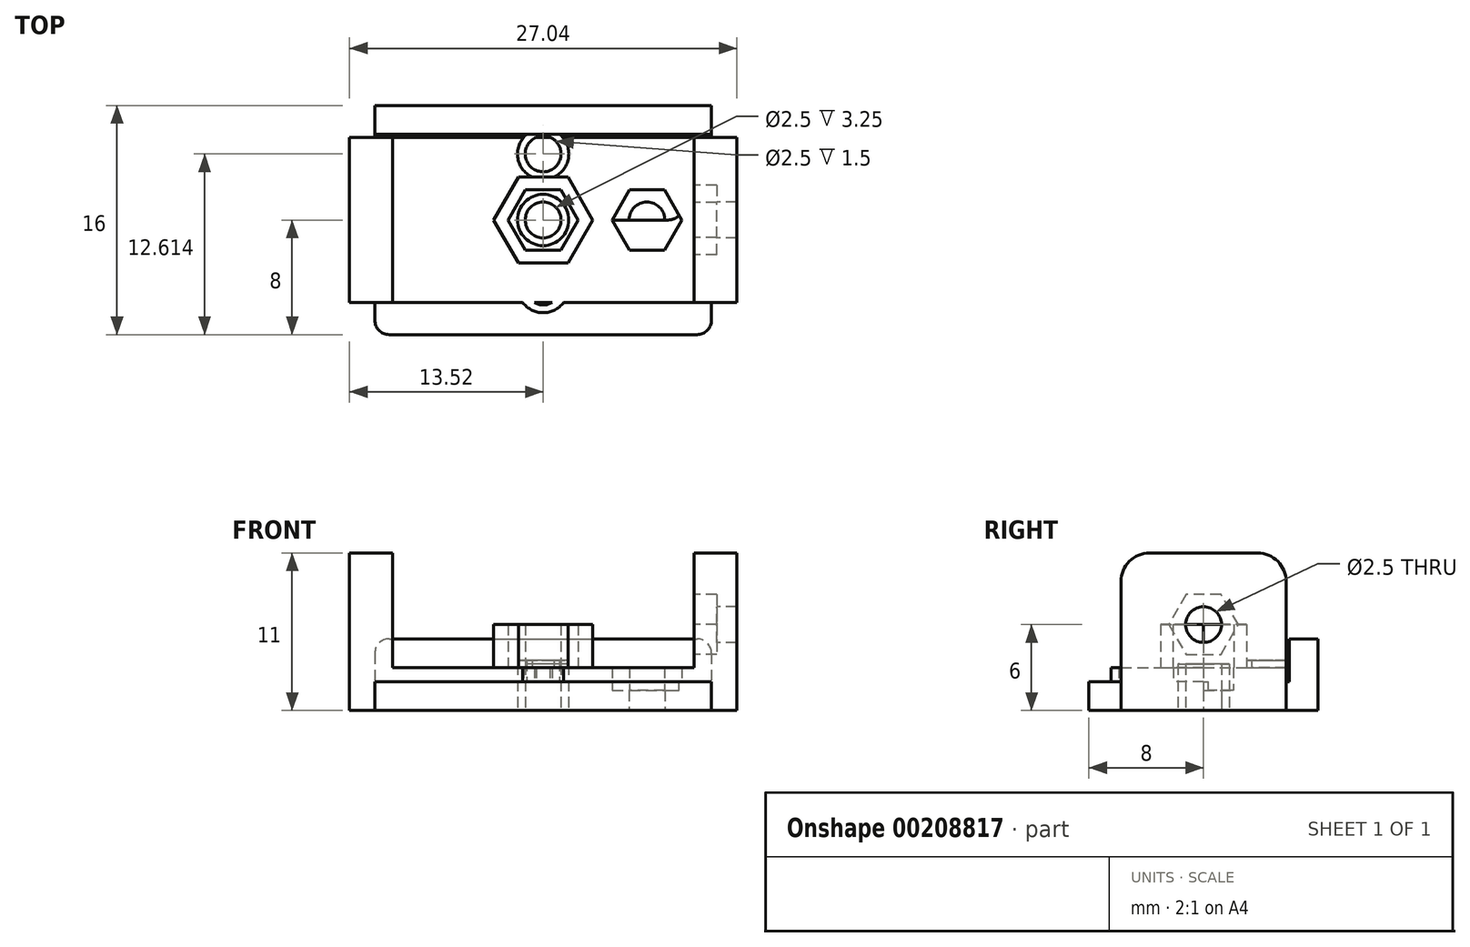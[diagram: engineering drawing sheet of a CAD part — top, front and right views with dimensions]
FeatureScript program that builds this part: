
annotation { "Feature Type Name" : "Feature", "Feature Type Description" : "" }
export const myFeature = defineFeature(function(context is Context, id is Id, definition is map)
    precondition{}
    {
        {
            var Q0;
            Q0=qCreatedBy(makeId("Top.planeOp"),FACE);
            var sketch = newSketch(context, id + "F0", { "sketchPlane" : qUnion([Q0])});
            skLineSegment(sketch, "E0.bottom", {"start": v(-11.75, 8) * mm, "end": v(11.75, 8) * mm});
            skLineSegment(sketch, "E0.top", {"start": v(-11.75, -8) * mm, "end": v(11.75, -8) * mm});
            skLineSegment(sketch, "E0.left", {"start": v(-11.75, 8) * mm, "end": v(-11.75, -8) * mm});
            skLineSegment(sketch, "E0.right", {"start": v(11.75, 8) * mm, "end": v(11.75, -8) * mm});
            skPoint(sketch, "E0.middle", {"position": v(0, 0) * mm});
            skLineSegment(sketch, "E1", {"start": v(-11.75, 6) * mm, "end": v(11.75, 6) * mm});
            skLineSegment(sketch, "E2.bottom", {"start": v(-9.75, 0) * mm, "end": v(9.75, 0) * mm});
            skLineSegment(sketch, "E2.top", {"start": v(-9.75, 2.5) * mm, "end": v(9.75, 2.5) * mm});
            skLineSegment(sketch, "E2.left", {"start": v(-9.75, 0) * mm, "end": v(-9.75, 2.5) * mm});
            skLineSegment(sketch, "E2.right", {"start": v(9.75, 0) * mm, "end": v(9.75, 2.5) * mm});
            skPoint(sketch, "E2.middle", {"position": v(0, 1.25) * mm});
            skCircle(sketch, "E3", {"center": v(0, 1.25) * mm, "radius": 1.1 * mm, "construction": true});
            skCircle(sketch, "E4", {"center": v(0, 1.25) * mm, "radius": 2.4 * mm, "construction": true});
            skCircle(sketch, "E5", {"center": v(0, 1.25) * mm, "radius": 1 * mm, "construction": true});
            skSolve(sketch);
        }
        {
            var Q0;
            {var subQ1=sQuery(id+"F0.wireOp",EDGE,"E0.top");Q0=makeQuery(id+"F0.imprint","IMPRINT",FACE,{"disambiguationData":[TD([[makeQuery(id+"F0.imprint","IMPRINT",EDGE,{"derivedFrom":subQ1}),1.0]])]});}
            extrude(context, id + "F1", {"entities" : qUnion([Q0]), "depth" : 2 * mm, "offsetDistance" : 25 * mm});
        }
        {
            var Q0;
            {var subQ0=sQuery(id+"F0.wireOp",EDGE,"E0.bottom");Q0=makeQuery(id+"F0.imprint","IMPRINT",FACE,{"disambiguationData":[TD([[makeQuery(id+"F0.imprint","IMPRINT",EDGE,{"derivedFrom":subQ0}),-1.0]])]});}
            extrude(context, id + "F2", {"entities" : qUnion([Q0]), "operationType" : NewBodyOperationType.ADD, "depth" : 5 * mm, "offsetDistance" : 25 * mm});
        }
        {
            var Q0;
            Q0=makeQuery(id+"F1.opExtrude","SWEPT_EDGE",EDGE,{"disambiguationData":[OSD([sQuery(id+"F0.wireOp",EDGE,"E2.top"),sQuery(id+"F0.wireOp",EDGE,"E2.left")])]});
            var Q1;
            Q1=makeQuery(id+"F1.opExtrude","SWEPT_EDGE",EDGE,{"disambiguationData":[OSD([sQuery(id+"F0.wireOp",EDGE,"E2.bottom"),sQuery(id+"F0.wireOp",EDGE,"E2.left")])]});
            var Q2;
            Q2=makeQuery(id+"F1.opExtrude","SWEPT_EDGE",EDGE,{"disambiguationData":[OSD([sQuery(id+"F0.wireOp",EDGE,"E2.top"),sQuery(id+"F0.wireOp",EDGE,"E2.right")])]});
            var Q3;
            Q3=makeQuery(id+"F1.opExtrude","SWEPT_EDGE",EDGE,{"disambiguationData":[OSD([sQuery(id+"F0.wireOp",EDGE,"E2.bottom"),sQuery(id+"F0.wireOp",EDGE,"E2.right")])]});
            var Q4;
            Q4=makeQuery(id+"F2.opExtrude","CAP_EDGE",EDGE,{"disambiguationData":[OSD([sQuery(id+"F0.wireOp",EDGE,"E0.right")])],"isStart":false});
            var Q5;
            Q5=makeQuery(id+"F2.opExtrude","CAP_EDGE",EDGE,{"disambiguationData":[OSD([sQuery(id+"F0.wireOp",EDGE,"E0.left")])],"isStart":false});
            var Q6;
            Q6=makeQuery(id+"F1.opExtrude","SWEPT_EDGE",EDGE,{"disambiguationData":[OSD([sQuery(id+"F0.wireOp",EDGE,"E0.top"),sQuery(id+"F0.wireOp",EDGE,"E0.left")])]});
            var Q7;
            Q7=makeQuery(id+"F1.opExtrude","SWEPT_EDGE",EDGE,{"disambiguationData":[OSD([sQuery(id+"F0.wireOp",EDGE,"E0.top"),sQuery(id+"F0.wireOp",EDGE,"E0.right")])]});
            fillet(context, id + "F3", {"entities" : qUnion([Q0, Q1, Q2, Q3, Q4, Q5, Q6, Q7]), "radius" : 1 * mm, "tangentPropagation" : true, "allowEdgeOverflow" : false});
        }
        {
            var Q0;
            Q0=qCreatedBy(makeId("Top.planeOp"),FACE);
            var sketch = newSketch(context, id + "F4", { "sketchPlane" : qUnion([Q0])});
            skLineSegment(sketch, "E6.bottom", {"start": v(-13.52, -5.77) * mm, "end": v(13.52, -5.77) * mm});
            skLineSegment(sketch, "E6.top", {"start": v(-13.52, 5.77) * mm, "end": v(13.52, 5.77) * mm});
            skLineSegment(sketch, "E6.left", {"start": v(-13.52, -5.77) * mm, "end": v(-13.52, 5.77) * mm});
            skLineSegment(sketch, "E6.right", {"start": v(13.52, -5.77) * mm, "end": v(13.52, 5.77) * mm});
            skPoint(sketch, "E6.middle", {"position": v(0, 0) * mm});
            skLineSegment(sketch, "E7", {"start": v(10.52, -5.77) * mm, "end": v(10.52, 5.77) * mm});
            skCircle(sketch, "E8", {"center": v(7.25, 0) * mm, "radius": 2.5 * mm, "construction": true});
            skCircle(sketch, "E9", {"center": v(7.25, 0) * mm, "radius": 1.25 * mm});
            skLineSegment(sketch, "E10.MirrorCS", {"start": v(-10.52, -5.77) * mm, "end": v(-10.52, 5.77) * mm});
            skCircle(sketch, "E11.cCircle", {"center": v(7.25, 0) * mm, "radius": 2.1 * mm, "construction": true});
            skLineSegment(sketch, "E11.0", {"start": v(8.46, -2.1) * mm, "end": v(6.03, -2.1) * mm});
            skLineSegment(sketch, "E11.1", {"start": v(6.03, -2.1) * mm, "end": v(4.82, 0) * mm});
            skLineSegment(sketch, "E11.2", {"start": v(4.82, 0) * mm, "end": v(6.03, 2.1) * mm});
            skLineSegment(sketch, "E11.3", {"start": v(6.03, 2.1) * mm, "end": v(8.46, 2.1) * mm});
            skLineSegment(sketch, "E11.4", {"start": v(8.46, 2.1) * mm, "end": v(9.67, 0) * mm});
            skLineSegment(sketch, "E11.5", {"start": v(9.67, 0) * mm, "end": v(8.46, -2.1) * mm});
            skPoint(sketch, "E11.0.midPoint", {"position": v(7.25, -2.1) * mm});
            skLineSegment(sketch, "E12", {"start": v(7.52, -5.77) * mm, "end": v(7.52, 5.77) * mm, "construction": true});
            skSolve(sketch);
        }
        {
            var Q0;
            {var subQ0=sQuery(id+"F4.wireOp",EDGE,"E7");Q0=makeQuery(id+"F4.imprint","IMPRINT",FACE,{"disambiguationData":[TD([[makeQuery(id+"F4.imprint","IMPRINT",EDGE,{"derivedFrom":subQ0}),1.0]])]});}
            extrude(context, id + "F5", {"entities" : qUnion([Q0]), "depth" : 3 * mm, "offsetDistance" : 25 * mm});
        }
        {
            var Q0;
            {var subQ0=sQuery(id+"F4.wireOp",EDGE,"E6.left");Q0=makeQuery(id+"F4.imprint","IMPRINT",FACE,{"disambiguationData":[TD([[makeQuery(id+"F4.imprint","IMPRINT",EDGE,{"derivedFrom":subQ0}),-1.0]])]});}
            var Q1;
            {var subQ0=sQuery(id+"F4.wireOp",EDGE,"E6.right");Q1=makeQuery(id+"F4.imprint","IMPRINT",FACE,{"disambiguationData":[TD([[makeQuery(id+"F4.imprint","IMPRINT",EDGE,{"derivedFrom":subQ0}),1.0]])]});}
            extrude(context, id + "F6", {"entities" : qUnion([Q0, Q1]), "operationType" : NewBodyOperationType.ADD, "depth" : 11 * mm, "offsetDistance" : 25 * mm});
        }
        {
            var Q0;
            Q0=makeQuery(id+"F6.opExtrude","SWEPT_FACE",FACE,{"disambiguationData":[OSD([sQuery(id+"F4.wireOp",EDGE,"E7")])]});
            var sketch = newSketch(context, id + "F7", { "sketchPlane" : qUnion([Q0])});
            skLineSegment(sketch, "E13.0", {"start": v(5.77, 3) * mm, "end": v(-5.77, 3) * mm});
            skCircle(sketch, "E14", {"center": v(0, 6) * mm, "radius": 2.5 * mm, "construction": true});
            skCircle(sketch, "E15", {"center": v(0, 6) * mm, "radius": 1.25 * mm});
            skLineSegment(sketch, "E16", {"start": v(-5.77, 11) * mm, "end": v(5.77, 11) * mm, "construction": true});
            skCircle(sketch, "E17.cCircle", {"center": v(0, 6) * mm, "radius": 2.1 * mm, "construction": true});
            skLineSegment(sketch, "E17.0", {"start": v(1.21, 3.9) * mm, "end": v(-1.21, 3.9) * mm});
            skLineSegment(sketch, "E17.1", {"start": v(-1.21, 3.9) * mm, "end": v(-2.42, 6) * mm});
            skLineSegment(sketch, "E17.2", {"start": v(-2.42, 6) * mm, "end": v(-1.21, 8.1) * mm});
            skLineSegment(sketch, "E17.3", {"start": v(-1.21, 8.1) * mm, "end": v(1.21, 8.1) * mm});
            skLineSegment(sketch, "E17.4", {"start": v(1.21, 8.1) * mm, "end": v(2.42, 6) * mm});
            skLineSegment(sketch, "E17.5", {"start": v(2.42, 6) * mm, "end": v(1.21, 3.9) * mm});
            skPoint(sketch, "E17.0.midPoint", {"position": v(0, 3.9) * mm});
            skSolve(sketch);
        }
        {
            var Q0;
            Q0=makeQuery(id+"F4.imprint","IMPRINT",FACE,{"disambiguationData":[TD([[makeQuery(id+"F4.imprint","IMPRINT",EDGE,{"derivedFrom":sQuery(id+"F4.wireOp",EDGE,"E9")}),-1.0]])]});
            extrude(context, id + "F8", {"entities" : qUnion([Q0]), "operationType" : NewBodyOperationType.ADD, "depth" : 1.4 * mm, "offsetDistance" : 25 * mm});
        }
        {
            var Q0;
            Q0=makeQuery(id+"F7.imprint","IMPRINT",FACE,{"disambiguationData":[TD([[makeQuery(id+"F7.imprint","IMPRINT",EDGE,{"derivedFrom":sQuery(id+"F7.wireOp",EDGE,"E15")}),1.0]])]});
            extrude(context, id + "F9", {"entities" : qUnion([Q0]), "operationType" : NewBodyOperationType.REMOVE, "endBound" : BoundingType.THROUGH_ALL, "oppositeDirection" : true, "depth" : 25 * mm, "offsetDistance" : 25 * mm});
        }
        {
            var Q0;
            Q0=makeQuery(id+"F7.imprint","IMPRINT",FACE,{"disambiguationData":[TD([[makeQuery(id+"F7.imprint","IMPRINT",EDGE,{"derivedFrom":sQuery(id+"F7.wireOp",EDGE,"E15")}),-1.0]])]});
            extrude(context, id + "F10", {"entities" : qUnion([Q0]), "operationType" : NewBodyOperationType.REMOVE, "oppositeDirection" : true, "depth" : 1.6 * mm, "offsetDistance" : 25 * mm});
        }
        {
            var Q0;
            {var subQ0=sQuery(id+"F4.wireOp",EDGE,"E6.bottom");Q0=makeQuery(id+"F6.opExtrude","CAP_EDGE",EDGE,{"disambiguationData":[OSD([subQ0]),TDD([makeQuery(id+"F4.imprint","IMPRINT",EDGE,{"disambiguationData":[TD([[makeQuery(id+"F4.imprint","INTERSECT",VERTEX,{"derivedFrom":[subQ0,sQuery(id+"F4.wireOp",EDGE,"E6.left")]}),-1.0]])],"derivedFrom":subQ0})])],"isStart":false});}
            var Q1;
            {var subQ0=sQuery(id+"F4.wireOp",EDGE,"E6.bottom");Q1=makeQuery(id+"F6.opExtrude","CAP_EDGE",EDGE,{"disambiguationData":[OSD([subQ0]),TDD([makeQuery(id+"F4.imprint","IMPRINT",EDGE,{"disambiguationData":[TD([[makeQuery(id+"F4.imprint","INTERSECT",VERTEX,{"derivedFrom":[subQ0,sQuery(id+"F4.wireOp",EDGE,"E6.right")]}),1.0]])],"derivedFrom":subQ0})])],"isStart":false});}
            var Q2;
            {var subQ0=sQuery(id+"F4.wireOp",EDGE,"E6.top");Q2=makeQuery(id+"F6.opExtrude","CAP_EDGE",EDGE,{"disambiguationData":[OSD([subQ0]),TDD([makeQuery(id+"F4.imprint","IMPRINT",EDGE,{"disambiguationData":[TD([[makeQuery(id+"F4.imprint","INTERSECT",VERTEX,{"derivedFrom":[subQ0,sQuery(id+"F4.wireOp",EDGE,"E6.right")]}),1.0]])],"derivedFrom":subQ0})])],"isStart":false});}
            var Q3;
            {var subQ0=sQuery(id+"F4.wireOp",EDGE,"E6.top");Q3=makeQuery(id+"F6.opExtrude","CAP_EDGE",EDGE,{"disambiguationData":[OSD([subQ0]),TDD([makeQuery(id+"F4.imprint","IMPRINT",EDGE,{"disambiguationData":[TD([[makeQuery(id+"F4.imprint","INTERSECT",VERTEX,{"derivedFrom":[subQ0,sQuery(id+"F4.wireOp",EDGE,"E6.left")]}),-1.0]])],"derivedFrom":subQ0})])],"isStart":false});}
            fillet(context, id + "F11", {"entities" : qUnion([Q0, Q1, Q2, Q3]), "radius" : 2 * mm, "tangentPropagation" : true, "allowEdgeOverflow" : false});
        }
        {
            var Q0;
            Q0=qCreatedBy(makeId("Top.planeOp"),FACE);
            var sketch = newSketch(context, id + "F12", { "sketchPlane" : qUnion([Q0])});
            skCircle(sketch, "E18", {"center": v(0, 4.61) * mm, "radius": 1.25 * mm});
            skCircle(sketch, "E19", {"center": v(0, 0) * mm, "radius": 1.25 * mm});
            skCircle(sketch, "E20", {"center": v(0, -4.68) * mm, "radius": 1.25 * mm});
            skCircle(sketch, "E21", {"center": v(0, -4.68) * mm, "radius": 1.8 * mm});
            skCircle(sketch, "E22", {"center": v(0, 0) * mm, "radius": 1.8 * mm});
            skCircle(sketch, "E23", {"center": v(0, 4.61) * mm, "radius": 1.8 * mm});
            skSolve(sketch);
        }
        {
            var Q0;
            Q0=makeQuery(id+"F12.imprint","IMPRINT",FACE,{"disambiguationData":[TD([[makeQuery(id+"F12.imprint","IMPRINT",EDGE,{"derivedFrom":sQuery(id+"F12.wireOp",EDGE,"E18")}),-1.0]])]});
            extrude(context, id + "F13", {"entities" : qUnion([Q0]), "depth" : 3.5 * mm, "offsetDistance" : 25 * mm});
        }
        {
            var Q0;
            Q0=makeQuery(id+"F12.imprint","IMPRINT",FACE,{"disambiguationData":[TD([[makeQuery(id+"F12.imprint","IMPRINT",EDGE,{"derivedFrom":sQuery(id+"F12.wireOp",EDGE,"E19")}),-1.0]])]});
            extrude(context, id + "F14", {"entities" : qUnion([Q0]), "depth" : 3.25 * mm, "offsetDistance" : 25 * mm});
        }
        {
            var Q0;
            Q0=makeQuery(id+"F12.imprint","IMPRINT",FACE,{"disambiguationData":[TD([[makeQuery(id+"F12.imprint","IMPRINT",EDGE,{"derivedFrom":sQuery(id+"F12.wireOp",EDGE,"E20")}),-1.0]])]});
            extrude(context, id + "F15", {"entities" : qUnion([Q0]), "depth" : 3 * mm, "offsetDistance" : 25 * mm});
        }
        {
            var Q0;
            Q0=qCreatedBy(makeId("Top.planeOp"),FACE);
            var sketch = newSketch(context, id + "F16", { "sketchPlane" : qUnion([Q0])});
            skCircle(sketch, "E24", {"center": v(0, 0) * mm, "radius": 1.5 * mm});
            skCircle(sketch, "E25.cCircle", {"center": v(0, 0) * mm, "radius": 2.45 * mm, "construction": true});
            skLineSegment(sketch, "E25.0", {"start": v(-2.45, 0) * mm, "end": v(-1.23, 2.12) * mm});
            skLineSegment(sketch, "E25.1", {"start": v(-1.23, 2.12) * mm, "end": v(1.23, 2.13) * mm});
            skLineSegment(sketch, "E25.2", {"start": v(1.23, 2.13) * mm, "end": v(2.45, 0) * mm});
            skLineSegment(sketch, "E25.3", {"start": v(2.45, 0) * mm, "end": v(1.23, -2.12) * mm});
            skLineSegment(sketch, "E25.4", {"start": v(1.23, -2.12) * mm, "end": v(-1.23, -2.12) * mm});
            skLineSegment(sketch, "E25.5", {"start": v(-1.23, -2.12) * mm, "end": v(-2.45, 0) * mm});
            skCircle(sketch, "E26.cCircle", {"center": v(0, 0) * mm, "radius": 3.46 * mm, "construction": true});
            skLineSegment(sketch, "E26.0", {"start": v(-3.46, 0) * mm, "end": v(-1.73, 3) * mm});
            skLineSegment(sketch, "E26.1", {"start": v(-1.73, 3) * mm, "end": v(1.73, 3) * mm});
            skLineSegment(sketch, "E26.2", {"start": v(1.73, 3) * mm, "end": v(3.46, 0) * mm});
            skLineSegment(sketch, "E26.3", {"start": v(3.46, 0) * mm, "end": v(1.73, -3) * mm});
            skLineSegment(sketch, "E26.4", {"start": v(1.73, -3) * mm, "end": v(-1.73, -3) * mm});
            skLineSegment(sketch, "E26.5", {"start": v(-1.73, -3) * mm, "end": v(-3.46, 0) * mm});
            skSolve(sketch);
        }
        {
            var Q0;
            Q0=makeQuery(id+"F16.imprint","IMPRINT",FACE,{"disambiguationData":[TD([[makeQuery(id+"F16.imprint","IMPRINT",EDGE,{"derivedFrom":sQuery(id+"F16.wireOp",EDGE,"E25.0")}),1.0]])]});
            var Q1;
            Q1=makeQuery(id+"F16.imprint","IMPRINT",FACE,{"disambiguationData":[TD([[makeQuery(id+"F16.imprint","IMPRINT",EDGE,{"derivedFrom":sQuery(id+"F16.wireOp",EDGE,"E24")}),-1.0]])]});
            extrude(context, id + "F17", {"entities" : qUnion([Q0, Q1]), "depth" : 3 * mm, "offsetDistance" : 25 * mm});
        }
        {
            var Q0;
            Q0=makeQuery(id+"F16.imprint","IMPRINT",FACE,{"disambiguationData":[TD([[makeQuery(id+"F16.imprint","IMPRINT",EDGE,{"derivedFrom":sQuery(id+"F16.wireOp",EDGE,"E25.0")}),1.0]])]});
            extrude(context, id + "F18", {"entities" : qUnion([Q0]), "operationType" : NewBodyOperationType.ADD, "depth" : 6 * mm, "offsetDistance" : 25 * mm});
        }
    });
